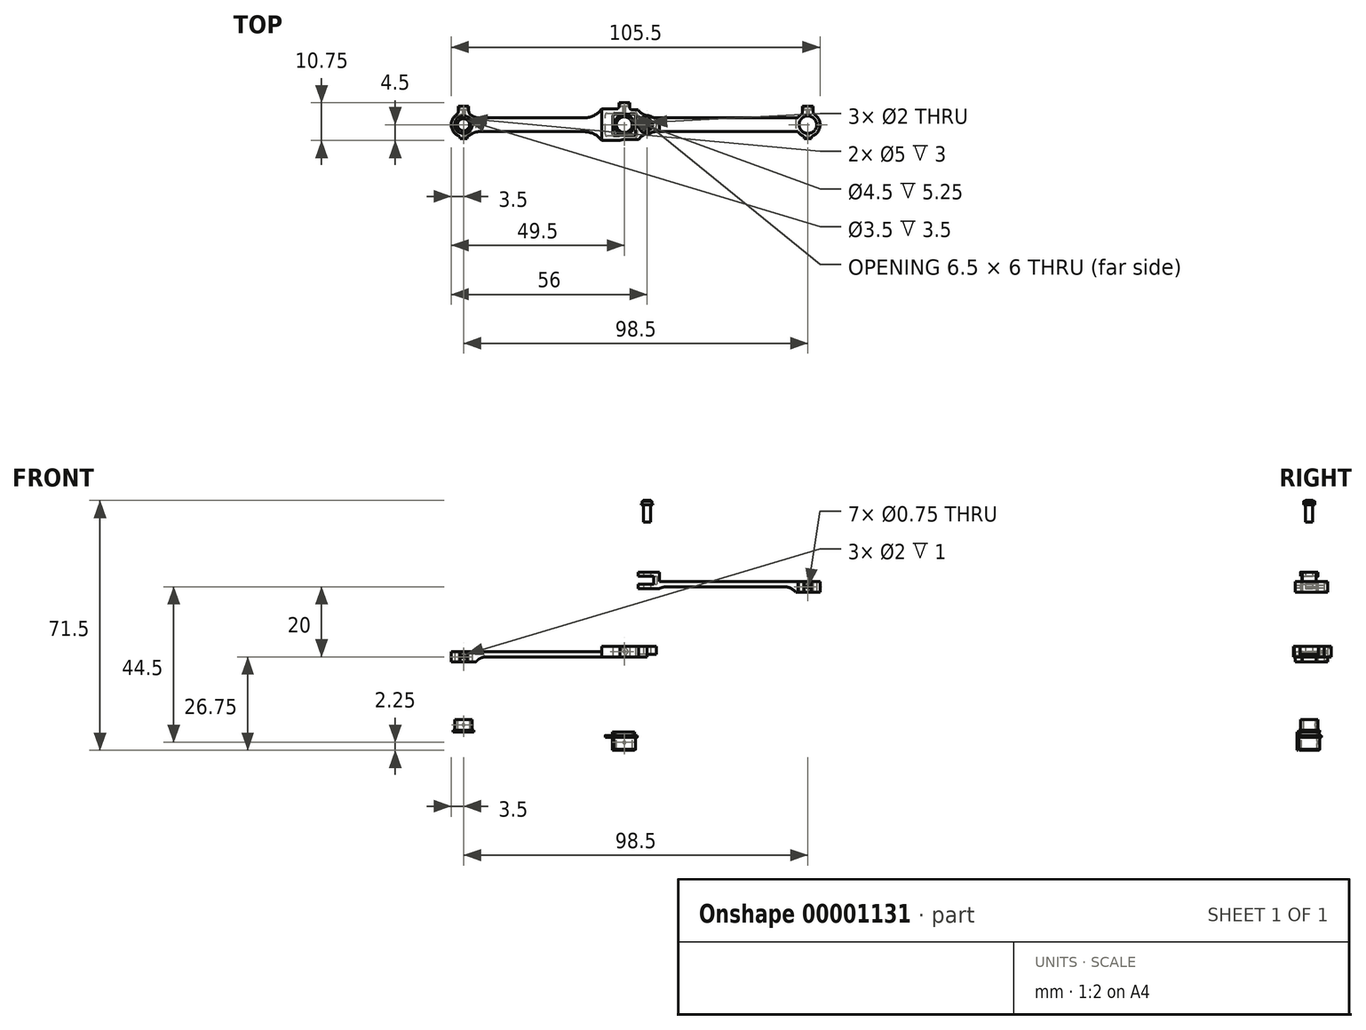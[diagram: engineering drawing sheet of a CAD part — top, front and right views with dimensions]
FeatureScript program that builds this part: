
annotation { "Feature Type Name" : "Feature", "Feature Type Description" : "" }
export const myFeature = defineFeature(function(context is Context, id is Id, definition is map)
    precondition{}
    {
        {
            var Q0;
            Q0=qCreatedBy(makeId("Top.planeOp"),FACE);
            var sketch = newSketch(context, id + "F0", { "sketchPlane" : qUnion([Q0])});
            skCircle(sketch, "E0", {"center": v(0, 0) * mm, "radius": 2.5 * mm});
            skCircle(sketch, "E1", {"center": v(46, 0) * mm, "radius": 2.25 * mm, "construction": true});
            skCircle(sketch, "E2", {"center": v(52.5, 0) * mm, "radius": 1 * mm});
            skArc(sketch, "E3", {"start": v(1, -3.35) * mm, "mid": v(2.05, -2.84) * mm, "end": v(2.87, -2) * mm});
            skCircle(sketch, "E4", {"center": v(52.5, 0) * mm, "radius": 2.62 * mm});
            skLineSegment(sketch, "E5", {"start": v(-1.5, 3.16) * mm, "end": v(-1.5, 5.25) * mm});
            skLineSegment(sketch, "E6", {"start": v(-1.5, 5.25) * mm, "end": v(1.5, 5.25) * mm});
            skLineSegment(sketch, "E7", {"start": v(1.5, 5.25) * mm, "end": v(1.5, 3.16) * mm});
            skLineSegment(sketch, "E8", {"start": v(42.75, 3) * mm, "end": v(49.25, 3) * mm});
            skLineSegment(sketch, "E9", {"start": v(49.25, 3) * mm, "end": v(49.25, -3) * mm});
            skLineSegment(sketch, "E10", {"start": v(49.25, -3) * mm, "end": v(42.75, -3) * mm});
            skLineSegment(sketch, "E11", {"start": v(42.75, -3) * mm, "end": v(42.75, 3) * mm});
            skLineSegment(sketch, "E12", {"start": v(52.5, 2.62) * mm, "end": v(52.5, 4.25) * mm});
            skLineSegment(sketch, "E13", {"start": v(52.5, 4.25) * mm, "end": v(47.5, 4.25) * mm});
            skLineSegment(sketch, "E14", {"start": v(39.5, 4.5) * mm, "end": v(39.5, 2) * mm});
            skLineSegment(sketch, "E15", {"start": v(39.5, -4.5) * mm, "end": v(44.75, -4.5) * mm});
            skLineSegment(sketch, "E16", {"start": v(52.5, -4.5) * mm, "end": v(52.5, -2.62) * mm});
            skLineSegment(sketch, "E17", {"start": v(2.87, 2) * mm, "end": v(39.5, 2) * mm});
            skLineSegment(sketch, "E18", {"start": v(2.87, -2) * mm, "end": v(39.5, -2) * mm});
            skLineSegment(sketch, "E19", {"start": v(44.5, 4.5) * mm, "end": v(44.5, 6.25) * mm});
            skLineSegment(sketch, "E20", {"start": v(44.5, 6.25) * mm, "end": v(47.5, 6.25) * mm});
            skLineSegment(sketch, "E21", {"start": v(47.5, 6.25) * mm, "end": v(47.5, 4.25) * mm});
            skLineSegment(sketch, "E22.trimOffspring", {"start": v(39.5, -2) * mm, "end": v(39.5, -4.5) * mm});
            skLineSegment(sketch, "E23", {"start": v(-1, -3.35) * mm, "end": v(-1, -4) * mm});
            skLineSegment(sketch, "E24", {"start": v(-1, -4) * mm, "end": v(1, -4) * mm});
            skLineSegment(sketch, "E25", {"start": v(1, -4) * mm, "end": v(1, -3.35) * mm});
            skArc(sketch, "E26.trimOffspring", {"start": v(2.87, 2) * mm, "mid": v(2.26, 2.67) * mm, "end": v(1.5, 3.16) * mm});
            skArc(sketch, "E27.trimOffspring", {"start": v(-1.5, 3.16) * mm, "mid": v(-3.49, -0.27) * mm, "end": v(-1, -3.35) * mm});
            skPoint(sketch, "E28", {"position": v(46, 6.25) * mm});
            skArc(sketch, "E29", {"start": v(50, 4.25) * mm, "mid": v(51.07, 3.16) * mm, "end": v(52.5, 2.63) * mm});
            skArc(sketch, "E30", {"start": v(52.5, -2.62) * mm, "mid": v(51.03, -3.27) * mm, "end": v(50, -4.5) * mm});
            skLineSegment(sketch, "E31", {"start": v(39.5, 4.5) * mm, "end": v(44.5, 4.5) * mm});
            skCircle(sketch, "E32", {"center": v(46, 0) * mm, "radius": 3 * mm, "construction": true});
            skLineSegment(sketch, "E33", {"start": v(50.14, -4.25) * mm, "end": v(46, -4.25) * mm});
            skArc(sketch, "E34", {"start": v(46, -4.25) * mm, "mid": v(45.36, -4.31) * mm, "end": v(44.75, -4.5) * mm});
            skLineSegment(sketch, "E35.trimOffspring", {"start": v(50, -4.5) * mm, "end": v(52.5, -4.5) * mm});
            skSolve(sketch);
        }
        {
            var Q0;
            Q0=makeQuery(id+"F0.imprint","IMPRINT",FACE,{"disambiguationData":[TD([[makeQuery(id+"F0.imprint","IMPRINT",EDGE,{"derivedFrom":sQuery(id+"F0.wireOp",EDGE,"E0")}),-1.0]])]});
            extrude(context, id + "F1", {"entities" : qUnion([Q0]), "depth" : 3 * mm});
        }
        {
            var Q0;
            Q0=makeQuery(id+"F1.opExtrude","SWEPT_EDGE",EDGE,{"disambiguationData":[OSD([sQuery(id+"F0.wireOp",EDGE,"E14"),sQuery(id+"F0.wireOp",EDGE,"E17")])]});
            var Q1;
            Q1=makeQuery(id+"F1.opExtrude","SWEPT_EDGE",EDGE,{"disambiguationData":[OSD([sQuery(id+"F0.wireOp",EDGE,"E18"),sQuery(id+"F0.wireOp",EDGE,"E22.trimOffspring")])]});
            fillet(context, id + "F2", {"entities" : qUnion([Q0, Q1]), "radius" : 6 * mm, "tangentPropagation" : true, "allowEdgeOverflow" : false});
        }
        {
            var Q0;
            Q0=makeQuery(id+"F0.imprint","IMPRINT",FACE,{"disambiguationData":[TD([[makeQuery(id+"F0.imprint","IMPRINT",EDGE,{"derivedFrom":sQuery(id+"F0.wireOp",EDGE,"E2")}),-1.0]])]});
            extrude(context, id + "F3", {"entities" : qUnion([Q0]), "operationType" : NewBodyOperationType.ADD, "depth" : 3 * mm});
        }
        {
            var Q0;
            Q0=makeQuery(id+"F1.opExtrude","SWEPT_EDGE",EDGE,{"disambiguationData":[OSD([sQuery(id+"F0.wireOp",EDGE,"E13"),sQuery(id+"F0.wireOp",EDGE,"E21")])]});
            var Q1;
            Q1=makeQuery(id+"F1.opExtrude","SWEPT_EDGE",EDGE,{"disambiguationData":[OSD([sQuery(id+"F0.wireOp",EDGE,"E19"),sQuery(id+"F0.wireOp",EDGE,"E31")])]});
            fillet(context, id + "F4", {"entities" : qUnion([Q0, Q1]), "radius" : 0.75 * mm, "tangentPropagation" : true, "allowEdgeOverflow" : false});
        }
        {
            var Q0;
            Q0=makeQuery(id+"F1.opExtrude","SWEPT_EDGE",EDGE,{"disambiguationData":[OSD([sQuery(id+"F0.wireOp",EDGE,"E3"),sQuery(id+"F0.wireOp",EDGE,"E25")])]});
            var Q1;
            Q1=makeQuery(id+"F1.opExtrude","SWEPT_EDGE",EDGE,{"disambiguationData":[OSD([sQuery(id+"F0.wireOp",EDGE,"E23"),sQuery(id+"F0.wireOp",EDGE,"E27.trimOffspring")])]});
            fillet(context, id + "F5", {"entities" : qUnion([Q0, Q1]), "radius" : 0.75 * mm, "tangentPropagation" : true, "allowEdgeOverflow" : false});
        }
        {
            var Q0;
            Q0=makeQuery(id+"F1.opExtrude","SWEPT_EDGE",EDGE,{"disambiguationData":[OSD([sQuery(id+"F0.wireOp",EDGE,"E7"),sQuery(id+"F0.wireOp",EDGE,"E26.trimOffspring")])]});
            var Q1;
            Q1=makeQuery(id+"F1.opExtrude","SWEPT_EDGE",EDGE,{"disambiguationData":[OSD([sQuery(id+"F0.wireOp",EDGE,"E5"),sQuery(id+"F0.wireOp",EDGE,"E27.trimOffspring")])]});
            fillet(context, id + "F6", {"entities" : qUnion([Q0, Q1]), "radius" : 1.25 * mm, "tangentPropagation" : true, "allowEdgeOverflow" : false});
        }
        {
            var Q0;
            Q0=makeQuery(id+"F1.opExtrude","SWEPT_EDGE",EDGE,{"disambiguationData":[OSD([sQuery(id+"F0.wireOp",EDGE,"E17"),sQuery(id+"F0.wireOp",EDGE,"E26.trimOffspring")])]});
            var Q1;
            Q1=makeQuery(id+"F1.opExtrude","SWEPT_EDGE",EDGE,{"disambiguationData":[OSD([sQuery(id+"F0.wireOp",EDGE,"E3"),sQuery(id+"F0.wireOp",EDGE,"E18")])]});
            fillet(context, id + "F7", {"entities" : qUnion([Q0, Q1]), "radius" : 3.5 * mm, "tangentPropagation" : true, "allowEdgeOverflow" : false});
        }
        {
            var Q0;
            Q0=makeQuery(id+"F1.opExtrude","SWEPT_EDGE",EDGE,{"disambiguationData":[OSD([sQuery(id+"F0.wireOp",EDGE,"E8"),sQuery(id+"F0.wireOp",EDGE,"E11")])]});
            var Q1;
            Q1=makeQuery(id+"F1.opExtrude","SWEPT_EDGE",EDGE,{"disambiguationData":[OSD([sQuery(id+"F0.wireOp",EDGE,"E8"),sQuery(id+"F0.wireOp",EDGE,"E9")])]});
            var Q2;
            Q2=makeQuery(id+"F1.opExtrude","SWEPT_EDGE",EDGE,{"disambiguationData":[OSD([sQuery(id+"F0.wireOp",EDGE,"E10"),sQuery(id+"F0.wireOp",EDGE,"E11")])]});
            var Q3;
            Q3=makeQuery(id+"F1.opExtrude","SWEPT_EDGE",EDGE,{"disambiguationData":[OSD([sQuery(id+"F0.wireOp",EDGE,"E9"),sQuery(id+"F0.wireOp",EDGE,"E10")])]});
            fillet(context, id + "F8", {"entities" : qUnion([Q0, Q1, Q2, Q3]), "radius" : 0.5 * mm, "tangentPropagation" : true, "allowEdgeOverflow" : false});
        }
        {
            var Q0;
            {var subQ0=sQuery(id+"F0.wireOp",EDGE,"E4");Q0=makeQuery(id+"F3.boolean.opBoolean","MERGE",FACE,{"derivedFrom":[makeQuery(id+"F1.opExtrude","CAP_FACE",FACE,{"disambiguationData":[OSD([sQuery(id+"F0.wireOp",EDGE,"E0"),sQuery(id+"F0.wireOp",EDGE,"E3"),subQ0,sQuery(id+"F0.wireOp",EDGE,"E5"),sQuery(id+"F0.wireOp",EDGE,"E6"),sQuery(id+"F0.wireOp",EDGE,"E7"),sQuery(id+"F0.wireOp",EDGE,"E8"),sQuery(id+"F0.wireOp",EDGE,"E9"),sQuery(id+"F0.wireOp",EDGE,"E10"),sQuery(id+"F0.wireOp",EDGE,"E11"),sQuery(id+"F0.wireOp",EDGE,"E13"),sQuery(id+"F0.wireOp",EDGE,"E14"),sQuery(id+"F0.wireOp",EDGE,"E15"),sQuery(id+"F0.wireOp",EDGE,"E17"),sQuery(id+"F0.wireOp",EDGE,"E18"),sQuery(id+"F0.wireOp",EDGE,"E19"),sQuery(id+"F0.wireOp",EDGE,"E20"),sQuery(id+"F0.wireOp",EDGE,"E21"),sQuery(id+"F0.wireOp",EDGE,"E22.trimOffspring"),sQuery(id+"F0.wireOp",EDGE,"E23"),sQuery(id+"F0.wireOp",EDGE,"E24"),sQuery(id+"F0.wireOp",EDGE,"E25"),sQuery(id+"F0.wireOp",EDGE,"E26.trimOffspring"),sQuery(id+"F0.wireOp",EDGE,"E27.trimOffspring"),sQuery(id+"F0.wireOp",EDGE,"E29"),sQuery(id+"F0.wireOp",EDGE,"E30"),sQuery(id+"F0.wireOp",EDGE,"E31"),sQuery(id+"F0.wireOp",EDGE,"E33"),sQuery(id+"F0.wireOp",EDGE,"E34")])],"isStart":true}),makeQuery(id+"F3.opExtrude","CAP_FACE",FACE,{"disambiguationData":[OSD([sQuery(id+"F0.wireOp",EDGE,"E2"),subQ0])],"isStart":true})]});}
            var sketch = newSketch(context, id + "F9", { "sketchPlane" : qUnion([Q0])});
            skLineSegment(sketch, "E36", {"start": v(3.5, -2.1) * mm, "end": v(3.5, 2.1) * mm});
            skSolve(sketch);
        }
        {
            var Q0;
            {var subQ26=sQuery(id+"F9.wireOp",EDGE,"E36");Q0=makeQuery(id+"F9.imprint","IMPRINT",FACE,{"disambiguationData":[TD([[makeQuery(id+"F9.imprint","IMPRINT",EDGE,{"derivedFrom":subQ26}),-1.0]])]});}
            extrude(context, id + "F10", {"entities" : qUnion([Q0]), "operationType" : NewBodyOperationType.REMOVE, "oppositeDirection" : true, "depth" : 1.5 * mm});
        }
        {
            var Q0;
            {var subQ0=sQuery(id+"F0.wireOp",EDGE,"E4");Q0=makeQuery(id+"F3.boolean.opBoolean","MERGE",FACE,{"derivedFrom":[makeQuery(id+"F1.opExtrude","CAP_FACE",FACE,{"disambiguationData":[OSD([sQuery(id+"F0.wireOp",EDGE,"E0"),sQuery(id+"F0.wireOp",EDGE,"E3"),subQ0,sQuery(id+"F0.wireOp",EDGE,"E5"),sQuery(id+"F0.wireOp",EDGE,"E6"),sQuery(id+"F0.wireOp",EDGE,"E7"),sQuery(id+"F0.wireOp",EDGE,"E8"),sQuery(id+"F0.wireOp",EDGE,"E9"),sQuery(id+"F0.wireOp",EDGE,"E10"),sQuery(id+"F0.wireOp",EDGE,"E11"),sQuery(id+"F0.wireOp",EDGE,"E13"),sQuery(id+"F0.wireOp",EDGE,"E14"),sQuery(id+"F0.wireOp",EDGE,"E15"),sQuery(id+"F0.wireOp",EDGE,"E17"),sQuery(id+"F0.wireOp",EDGE,"E18"),sQuery(id+"F0.wireOp",EDGE,"E19"),sQuery(id+"F0.wireOp",EDGE,"E20"),sQuery(id+"F0.wireOp",EDGE,"E21"),sQuery(id+"F0.wireOp",EDGE,"E22.trimOffspring"),sQuery(id+"F0.wireOp",EDGE,"E23"),sQuery(id+"F0.wireOp",EDGE,"E24"),sQuery(id+"F0.wireOp",EDGE,"E25"),sQuery(id+"F0.wireOp",EDGE,"E26.trimOffspring"),sQuery(id+"F0.wireOp",EDGE,"E27.trimOffspring"),sQuery(id+"F0.wireOp",EDGE,"E29"),sQuery(id+"F0.wireOp",EDGE,"E30"),sQuery(id+"F0.wireOp",EDGE,"E31"),sQuery(id+"F0.wireOp",EDGE,"E33"),sQuery(id+"F0.wireOp",EDGE,"E34")])],"isStart":false}),makeQuery(id+"F3.opExtrude","CAP_FACE",FACE,{"disambiguationData":[OSD([sQuery(id+"F0.wireOp",EDGE,"E2"),subQ0])],"isStart":false})]});}
            var sketch = newSketch(context, id + "F11", { "sketchPlane" : qUnion([Q0])});
            skLineSegment(sketch, "E37", {"start": v(39.5, -4.5) * mm, "end": v(39.5, 4.5) * mm});
            skSolve(sketch);
        }
        {
            var Q0;
            Q0=makeQuery(id+"F11.imprint","IMPRINT",FACE,{"disambiguationData":[TD([[makeQuery(id+"F11.imprint","IMPRINT",EDGE,{"derivedFrom":sQuery(id+"F11.wireOp",EDGE,"E37")}),-1.0]])]});
            extrude(context, id + "F12", {"entities" : qUnion([Q0]), "operationType" : NewBodyOperationType.ADD, "depth" : 1.5 * mm});
        }
        {
            var Q0;
            Q0=makeQuery(id+"F10.boolean.opBoolean","COPY",EDGE,{"derivedFrom":makeQuery(id+"F10.opExtrude","CAP_EDGE",EDGE,{"disambiguationData":[OSD([sQuery(id+"F9.wireOp",EDGE,"E36")])],"isStart":false})});
            var Q1;
            Q1=makeQuery(id+"F12.opExtrude","CAP_EDGE",EDGE,{"disambiguationData":[OSD([sQuery(id+"F11.wireOp",EDGE,"E37")])],"isStart":true});
            fillet(context, id + "F13", {"entities" : qUnion([Q0, Q1]), "radius" : 4 * mm, "tangentPropagation" : true, "allowEdgeOverflow" : false});
        }
        {
            var Q0;
            Q0=makeQuery(id+"F0.imprint","IMPRINT",FACE,{"disambiguationData":[TD([[makeQuery(id+"F0.imprint","IMPRINT",EDGE,{"derivedFrom":sQuery(id+"F0.wireOp",EDGE,"E2")}),-1.0]])]});
            extrude(context, id + "F14", {"entities" : qUnion([Q0]), "operationType" : NewBodyOperationType.REMOVE, "depth" : 2.25 * mm});
        }
        {
            var Q0;
            Q0=makeQuery(id+"F1.opExtrude","SWEPT_FACE",FACE,{"disambiguationData":[OSD([sQuery(id+"F0.wireOp",EDGE,"E6")])]});
            var sketch = newSketch(context, id + "F15", { "sketchPlane" : qUnion([Q0])});
            skPoint(sketch, "E38", {"position": v(1.5, 1.5) * mm});
            skPoint(sketch, "E39", {"position": v(0, 0) * mm});
            skCircle(sketch, "E40", {"center": v(0, 1.5) * mm, "radius": 1 * mm});
            skSolve(sketch);
        }
        {
            var Q0;
            Q0=makeQuery(id+"F15.imprint","IMPRINT",FACE,{"disambiguationData":[TD([[makeQuery(id+"F15.imprint","IMPRINT",EDGE,{"derivedFrom":sQuery(id+"F15.wireOp",EDGE,"E40")}),1.0]])]});
            extrude(context, id + "F16", {"entities" : qUnion([Q0]), "operationType" : NewBodyOperationType.REMOVE, "oppositeDirection" : true, "depth" : 1 * mm});
        }
        {
            var Q0;
            {var subQ0=sQuery(id+"F0.wireOp",EDGE,"E20");Q0=makeQuery(id+"F12.boolean.opBoolean","MERGE",FACE,{"derivedFrom":[makeQuery(id+"F1.opExtrude","SWEPT_FACE",FACE,{"disambiguationData":[OSD([subQ0])]}),makeQuery(id+"F12.opExtrude","SWEPT_FACE",FACE,{"disambiguationData":[OSD([subQ0])]})]});}
            var sketch = newSketch(context, id + "F17", { "sketchPlane" : qUnion([Q0])});
            skPoint(sketch, "E41", {"position": v(-46, 1.5) * mm});
            skPoint(sketch, "E42", {"position": v(-44.5, 3) * mm});
            skCircle(sketch, "E43", {"center": v(-46, 3) * mm, "radius": 1 * mm});
            skCircle(sketch, "E44", {"center": v(-46, 3) * mm, "radius": 0.38 * mm});
            skSolve(sketch);
        }
        {
            var Q0;
            Q0=makeQuery(id+"F17.imprint","IMPRINT",FACE,{"disambiguationData":[TD([[makeQuery(id+"F17.imprint","IMPRINT",EDGE,{"derivedFrom":sQuery(id+"F17.wireOp",EDGE,"E43")}),1.0]])]});
            extrude(context, id + "F18", {"entities" : qUnion([Q0]), "operationType" : NewBodyOperationType.REMOVE, "oppositeDirection" : true, "depth" : 1 * mm});
        }
        {
            var Q0;
            Q0=makeQuery(id+"F1.opExtrude","SWEPT_FACE",FACE,{"disambiguationData":[OSD([sQuery(id+"F0.wireOp",EDGE,"E24")])]});
            var sketch = newSketch(context, id + "F19", { "sketchPlane" : qUnion([Q0])});
            skPoint(sketch, "E45", {"position": v(-1, 1.5) * mm});
            skPoint(sketch, "E46", {"position": v(0, 3) * mm});
            skCircle(sketch, "E47", {"center": v(0, 1.5) * mm, "radius": 0.38 * mm});
            skSolve(sketch);
        }
        {
            var Q0;
            Q0=makeQuery(id+"F19.imprint","IMPRINT",FACE,{"disambiguationData":[TD([[makeQuery(id+"F19.imprint","IMPRINT",EDGE,{"derivedFrom":sQuery(id+"F19.wireOp",EDGE,"E47")}),1.0]])]});
            extrude(context, id + "F20", {"entities" : qUnion([Q0]), "operationType" : NewBodyOperationType.REMOVE, "oppositeDirection" : true, "depth" : 25 * mm});
        }
        {
            var Q0;
            {var subQ0=sQuery(id+"F0.wireOp",EDGE,"E20");Q0=makeQuery(id+"F18.boolean.opBoolean","SPLIT",FACE,{"disambiguationData":[TD([makeQuery(id+"F18.opExtrude","SWEPT_FACE",FACE,{"disambiguationData":[OSD([sQuery(id+"F17.wireOp",EDGE,"E44")])]})])],"derivedFrom":makeQuery(id+"F12.boolean.opBoolean","MERGE",FACE,{"derivedFrom":[makeQuery(id+"F1.opExtrude","SWEPT_FACE",FACE,{"disambiguationData":[OSD([subQ0])]}),makeQuery(id+"F12.opExtrude","SWEPT_FACE",FACE,{"disambiguationData":[OSD([subQ0])]})]})});}
            extrude(context, id + "F21", {"entities" : qUnion([Q0]), "operationType" : NewBodyOperationType.REMOVE, "endBound" : BoundingType.UP_TO_NEXT, "oppositeDirection" : true, "depth" : 25 * mm});
        }
        {
            var Q0;
            Q0=qCreatedBy(makeId("Top.planeOp"),FACE);
            cPlane(context, id + "F22", {"entities" : qUnion([Q0]), "cplaneType" : CPlaneType.OFFSET, "offset" : 20 * mm, "width" : 150 * mm, "height" : 150 * mm});
        }
        {
            var Q0;
            Q0=qCreatedBy(makeId("Top.planeOp"),FACE);
            cPlane(context, id + "F23", {"entities" : qUnion([Q0]), "cplaneType" : CPlaneType.OFFSET, "offset" : 20 * mm, "oppositeDirection" : true, "width" : 150 * mm, "height" : 150 * mm});
        }
        {
            var Q0;
            Q0=qCreatedBy(id+"F23.planeOp",FACE);
            var sketch = newSketch(context, id + "F24", { "sketchPlane" : qUnion([Q0])});
            skCircle(sketch, "E48", {"center": v(0, 0) * mm, "radius": 3 * mm});
            skCircle(sketch, "E49", {"center": v(0, 0) * mm, "radius": 2.5 * mm});
            skCircle(sketch, "E50", {"center": v(0, 0) * mm, "radius": 1.75 * mm});
            skSolve(sketch);
        }
        {
            var Q0;
            Q0=makeQuery(id+"F24.imprint","IMPRINT",FACE,{"disambiguationData":[TD([[makeQuery(id+"F24.imprint","IMPRINT",EDGE,{"derivedFrom":sQuery(id+"F24.wireOp",EDGE,"E49")}),1.0]])]});
            extrude(context, id + "F25", {"entities" : qUnion([Q0]), "depth" : 3.5 * mm});
        }
        {
            var Q0;
            Q0=makeQuery(id+"F24.imprint","IMPRINT",FACE,{"disambiguationData":[TD([[makeQuery(id+"F24.imprint","IMPRINT",EDGE,{"derivedFrom":sQuery(id+"F24.wireOp",EDGE,"E48")}),1.0]])]});
            extrude(context, id + "F26", {"entities" : qUnion([Q0]), "operationType" : NewBodyOperationType.ADD, "depth" : 0.5 * mm});
        }
        {
            var Q0;
            Q0=qCreatedBy(makeId("Front.planeOp"),FACE);
            var sketch = newSketch(context, id + "F27", { "sketchPlane" : qUnion([Q0])});
            skLineSegment(sketch, "E51", {"start": v(0, 0) * mm, "end": v(0, -18) * mm, "construction": true});
            skCircle(sketch, "E52", {"center": v(0, -18) * mm, "radius": 0.38 * mm});
            skSolve(sketch);
        }
        {
            var Q0;
            Q0=makeQuery(id+"F27.imprint","IMPRINT",FACE,{"disambiguationData":[TD([[makeQuery(id+"F27.imprint","IMPRINT",EDGE,{"derivedFrom":sQuery(id+"F27.wireOp",EDGE,"E52")}),1.0]])]});
            extrude(context, id + "F28", {"entities" : qUnion([Q0]), "operationType" : NewBodyOperationType.REMOVE, "oppositeDirection" : true, "depth" : 25 * mm});
        }
        {
            var Q0;
            Q0=qCreatedBy(id+"F22.planeOp",FACE);
            var sketch = newSketch(context, id + "F29", { "sketchPlane" : qUnion([Q0])});
            skLineSegment(sketch, "E53", {"start": v(0, 0) * mm, "end": v(52.5, 0) * mm, "construction": true});
            skLineSegment(sketch, "E54", {"start": v(52.5, 0) * mm, "end": v(98.5, 0) * mm, "construction": true});
            skCircle(sketch, "E55", {"center": v(52.5, 0) * mm, "radius": 1 * mm});
            skCircle(sketch, "E56", {"center": v(98.5, 0) * mm, "radius": 2.5 * mm});
            skArc(sketch, "E57", {"start": v(54, 2) * mm, "mid": v(50, 0) * mm, "end": v(54, -2) * mm});
            skArc(sketch, "E58", {"start": v(95.63, -2) * mm, "mid": v(96.45, -2.84) * mm, "end": v(97.5, -3.35) * mm});
            skLineSegment(sketch, "E59", {"start": v(54, 2) * mm, "end": v(95.63, 2) * mm});
            skLineSegment(sketch, "E60", {"start": v(54, -2) * mm, "end": v(95.63, -2) * mm});
            skLineSegment(sketch, "E61", {"start": v(97.5, -3.35) * mm, "end": v(97.5, -4) * mm});
            skLineSegment(sketch, "E62", {"start": v(97.5, -4) * mm, "end": v(99.5, -4) * mm});
            skLineSegment(sketch, "E63", {"start": v(99.5, -4) * mm, "end": v(99.5, -3.35) * mm});
            skLineSegment(sketch, "E64", {"start": v(97, 3.16) * mm, "end": v(97, 5.25) * mm});
            skLineSegment(sketch, "E65", {"start": v(97, 5.25) * mm, "end": v(100, 5.25) * mm});
            skLineSegment(sketch, "E66", {"start": v(100, 5.25) * mm, "end": v(100, 3.16) * mm});
            skPoint(sketch, "E67", {"position": v(98.5, -4) * mm});
            skPoint(sketch, "E68", {"position": v(98.5, 5.25) * mm});
            skArc(sketch, "E69.trimOffspring", {"start": v(99.5, -3.35) * mm, "mid": v(101.99, -0.27) * mm, "end": v(100, 3.16) * mm});
            skArc(sketch, "E70.trimOffspring", {"start": v(97, 3.16) * mm, "mid": v(96.24, 2.67) * mm, "end": v(95.63, 2) * mm});
            skSolve(sketch);
        }
        {
            var Q0;
            Q0=makeQuery(id+"F29.imprint","IMPRINT",FACE,{"disambiguationData":[TD([[makeQuery(id+"F29.imprint","IMPRINT",EDGE,{"derivedFrom":sQuery(id+"F29.wireOp",EDGE,"E55")}),-1.0]])]});
            extrude(context, id + "F30", {"entities" : qUnion([Q0]), "depth" : 3 * mm});
        }
        {
            var Q0;
            Q0=makeQuery(id+"F29.imprint","IMPRINT",FACE,{"disambiguationData":[TD([[makeQuery(id+"F29.imprint","IMPRINT",EDGE,{"derivedFrom":sQuery(id+"F29.wireOp",EDGE,"E55")}),-1.0]])]});
            var sketch = newSketch(context, id + "F31", { "sketchPlane" : qUnion([Q0])});
            skLineSegment(sketch, "E71", {"start": v(95, 2) * mm, "end": v(95, -2) * mm});
            skLineSegment(sketch, "E72", {"start": v(56, 2) * mm, "end": v(56, -2) * mm});
            skSolve(sketch);
        }
        {
            var Q0;
            {var subQ2=sQuery(id+"F31.wireOp",EDGE,"E71");Q0=makeQuery(id+"F31.imprint","IMPRINT",FACE,{"disambiguationData":[TD([[makeQuery(id+"F31.imprint","IMPRINT",EDGE,{"derivedFrom":subQ2}),-1.0]])]});}
            extrude(context, id + "F32", {"entities" : qUnion([Q0]), "operationType" : NewBodyOperationType.REMOVE, "depth" : 1.5 * mm});
        }
        {
            var Q0;
            Q0=makeQuery(id+"F30.opExtrude","CAP_FACE",FACE,{"disambiguationData":[OSD([sQuery(id+"F29.wireOp",EDGE,"E55"),sQuery(id+"F29.wireOp",EDGE,"E56"),sQuery(id+"F29.wireOp",EDGE,"E57"),sQuery(id+"F29.wireOp",EDGE,"E58"),sQuery(id+"F29.wireOp",EDGE,"E59"),sQuery(id+"F29.wireOp",EDGE,"E60"),sQuery(id+"F29.wireOp",EDGE,"E61"),sQuery(id+"F29.wireOp",EDGE,"E62"),sQuery(id+"F29.wireOp",EDGE,"E63"),sQuery(id+"F29.wireOp",EDGE,"E64"),sQuery(id+"F29.wireOp",EDGE,"E65"),sQuery(id+"F29.wireOp",EDGE,"E66"),sQuery(id+"F29.wireOp",EDGE,"E69.trimOffspring"),sQuery(id+"F29.wireOp",EDGE,"E70.trimOffspring")])],"isStart":false});
            var sketch = newSketch(context, id + "F33", { "sketchPlane" : qUnion([Q0])});
            skLineSegment(sketch, "E73", {"start": v(56, -2) * mm, "end": v(56, 2) * mm});
            skSolve(sketch);
        }
        {
            var Q0;
            {var subQ0=sQuery(id+"F29.wireOp",EDGE,"E55");var subQ1=sQuery(id+"F29.wireOp",EDGE,"E57");var subQ2=sQuery(id+"F29.wireOp",EDGE,"E59");var subQ3=sQuery(id+"F29.wireOp",EDGE,"E60");Q0=makeQuery(id+"F32.boolean.opBoolean","SPLIT",FACE,{"disambiguationData":[TD([makeQuery(id+"F30.opExtrude","SWEPT_FACE",FACE,{"disambiguationData":[OSD([subQ0])]})])],"derivedFrom":makeQuery(id+"F30.opExtrude","CAP_FACE",FACE,{"disambiguationData":[OSD([subQ0,sQuery(id+"F29.wireOp",EDGE,"E56"),subQ1,sQuery(id+"F29.wireOp",EDGE,"E58"),subQ2,subQ3,sQuery(id+"F29.wireOp",EDGE,"E61"),sQuery(id+"F29.wireOp",EDGE,"E62"),sQuery(id+"F29.wireOp",EDGE,"E63"),sQuery(id+"F29.wireOp",EDGE,"E64"),sQuery(id+"F29.wireOp",EDGE,"E65"),sQuery(id+"F29.wireOp",EDGE,"E66"),sQuery(id+"F29.wireOp",EDGE,"E69.trimOffspring"),sQuery(id+"F29.wireOp",EDGE,"E70.trimOffspring")])],"isStart":true})});}
            extrude(context, id + "F34", {"entities" : qUnion([Q0]), "operationType" : NewBodyOperationType.REMOVE, "oppositeDirection" : true, "depth" : 1 * mm});
        }
        {
            var Q0;
            {var subQ1=sQuery(id+"F33.wireOp",EDGE,"E73");Q0=makeQuery(id+"F33.imprint","IMPRINT",FACE,{"disambiguationData":[TD([[makeQuery(id+"F33.imprint","IMPRINT",EDGE,{"derivedFrom":subQ1}),1.0]])]});}
            extrude(context, id + "F35", {"entities" : qUnion([Q0]), "operationType" : NewBodyOperationType.ADD, "depth" : 2.75 * mm});
        }
        {
            var Q0;
            Q0=makeQuery(id+"F32.boolean.opBoolean","COPY",EDGE,{"derivedFrom":makeQuery(id+"F32.opExtrude","CAP_EDGE",EDGE,{"disambiguationData":[OSD([sQuery(id+"F31.wireOp",EDGE,"E72")])],"isStart":false})});
            var Q1;
            Q1=makeQuery(id+"F32.boolean.opBoolean","COPY",EDGE,{"derivedFrom":makeQuery(id+"F32.opExtrude","CAP_EDGE",EDGE,{"disambiguationData":[OSD([sQuery(id+"F31.wireOp",EDGE,"E71")])],"isStart":false})});
            var Q2;
            Q2=makeQuery(id+"F35.opExtrude","CAP_EDGE",EDGE,{"disambiguationData":[OSD([sQuery(id+"F33.wireOp",EDGE,"E73")])],"isStart":true});
            fillet(context, id + "F36", {"entities" : qUnion([Q0, Q1, Q2]), "radius" : 4 * mm, "tangentPropagation" : true, "allowEdgeOverflow" : false});
        }
        {
            var Q0;
            Q0=makeQuery(id+"F30.opExtrude","CAP_FACE",FACE,{"disambiguationData":[OSD([sQuery(id+"F29.wireOp",EDGE,"E55"),sQuery(id+"F29.wireOp",EDGE,"E56"),sQuery(id+"F29.wireOp",EDGE,"E57"),sQuery(id+"F29.wireOp",EDGE,"E58"),sQuery(id+"F29.wireOp",EDGE,"E59"),sQuery(id+"F29.wireOp",EDGE,"E60"),sQuery(id+"F29.wireOp",EDGE,"E61"),sQuery(id+"F29.wireOp",EDGE,"E62"),sQuery(id+"F29.wireOp",EDGE,"E63"),sQuery(id+"F29.wireOp",EDGE,"E64"),sQuery(id+"F29.wireOp",EDGE,"E65"),sQuery(id+"F29.wireOp",EDGE,"E66"),sQuery(id+"F29.wireOp",EDGE,"E69.trimOffspring"),sQuery(id+"F29.wireOp",EDGE,"E70.trimOffspring")])],"isStart":false});
            var sketch = newSketch(context, id + "F37", { "sketchPlane" : qUnion([Q0])});
            skCircle(sketch, "E74", {"center": v(52.5, 0) * mm, "radius": 2.75 * mm});
            skSolve(sketch);
        }
        {
            var Q0;
            Q0=makeQuery(id+"F37.imprint","IMPRINT",FACE,{"disambiguationData":[TD([[makeQuery(id+"F37.imprint","IMPRINT",EDGE,{"derivedFrom":sQuery(id+"F37.wireOp",EDGE,"E74")}),1.0]])]});
            extrude(context, id + "F38", {"entities" : qUnion([Q0]), "operationType" : NewBodyOperationType.REMOVE, "depth" : 1.5 * mm});
        }
        {
            var Q0;
            Q0=makeQuery(id+"F37.imprint","IMPRINT",FACE,{"disambiguationData":[TD([[makeQuery(id+"F37.imprint","IMPRINT",EDGE,{"derivedFrom":sQuery(id+"F37.wireOp",EDGE,"E74")}),1.0]])]});
            extrude(context, id + "F39", {"entities" : qUnion([Q0]), "operationType" : NewBodyOperationType.REMOVE, "oppositeDirection" : true, "depth" : 0.75 * mm});
        }
        {
            var Q0;
            Q0=makeQuery(id+"F30.opExtrude","SWEPT_EDGE",EDGE,{"disambiguationData":[OSD([sQuery(id+"F29.wireOp",EDGE,"E58"),sQuery(id+"F29.wireOp",EDGE,"E61")])]});
            var Q1;
            Q1=makeQuery(id+"F30.opExtrude","SWEPT_EDGE",EDGE,{"disambiguationData":[OSD([sQuery(id+"F29.wireOp",EDGE,"E63"),sQuery(id+"F29.wireOp",EDGE,"E69.trimOffspring")])]});
            fillet(context, id + "F40", {"entities" : qUnion([Q0, Q1]), "radius" : 0.75 * mm, "tangentPropagation" : true, "allowEdgeOverflow" : false});
        }
        {
            var Q0;
            Q0=makeQuery(id+"F30.opExtrude","SWEPT_EDGE",EDGE,{"disambiguationData":[OSD([sQuery(id+"F29.wireOp",EDGE,"E66"),sQuery(id+"F29.wireOp",EDGE,"E69.trimOffspring")])]});
            var Q1;
            Q1=makeQuery(id+"F30.opExtrude","SWEPT_EDGE",EDGE,{"disambiguationData":[OSD([sQuery(id+"F29.wireOp",EDGE,"E64"),sQuery(id+"F29.wireOp",EDGE,"E70.trimOffspring")])]});
            fillet(context, id + "F41", {"entities" : qUnion([Q0, Q1]), "radius" : 1.25 * mm, "tangentPropagation" : true, "allowEdgeOverflow" : false});
        }
        {
            var Q0;
            {var subQ0=sQuery(id+"F29.wireOp",EDGE,"E57");var subQ1=sQuery(id+"F29.wireOp",EDGE,"E59");Q0=makeQuery(id+"F38.boolean.opBoolean","SPLIT",EDGE,{"disambiguationData":[TD([makeQuery(id+"F38.opExtrude","CAP_FACE",FACE,{"disambiguationData":[OSD([sQuery(id+"F37.wireOp",EDGE,"E74")])],"isStart":false})])],"derivedFrom":makeQuery(id+"F35.boolean.opBoolean","MERGE",EDGE,{"derivedFrom":[makeQuery(id+"F30.opExtrude","SWEPT_EDGE",EDGE,{"disambiguationData":[OSD([subQ0,subQ1])]}),makeQuery(id+"F35.opExtrude","SWEPT_EDGE",EDGE,{"disambiguationData":[OSD([subQ0,subQ1])]})]})});}
            var Q1;
            {var subQ0=sQuery(id+"F29.wireOp",EDGE,"E57");var subQ1=sQuery(id+"F29.wireOp",EDGE,"E60");Q1=makeQuery(id+"F38.boolean.opBoolean","SPLIT",EDGE,{"disambiguationData":[TD([makeQuery(id+"F38.opExtrude","CAP_FACE",FACE,{"disambiguationData":[OSD([sQuery(id+"F37.wireOp",EDGE,"E74")])],"isStart":false})])],"derivedFrom":makeQuery(id+"F35.boolean.opBoolean","MERGE",EDGE,{"derivedFrom":[makeQuery(id+"F30.opExtrude","SWEPT_EDGE",EDGE,{"disambiguationData":[OSD([subQ0,subQ1])]}),makeQuery(id+"F35.opExtrude","SWEPT_EDGE",EDGE,{"disambiguationData":[OSD([subQ0,subQ1])]})]})});}
            fillet(context, id + "F42", {"entities" : qUnion([Q0, Q1]), "radius" : 3.5 * mm, "tangentPropagation" : true, "allowEdgeOverflow" : false});
        }
        {
            var Q0;
            Q0=makeQuery(id+"F30.opExtrude","SWEPT_FACE",FACE,{"disambiguationData":[OSD([sQuery(id+"F29.wireOp",EDGE,"E65")])]});
            var sketch = newSketch(context, id + "F43", { "sketchPlane" : qUnion([Q0])});
            skPoint(sketch, "E75", {"position": v(-98.5, 23) * mm});
            skPoint(sketch, "E76", {"position": v(-100, 21.5) * mm});
            skCircle(sketch, "E77", {"center": v(-98.5, 21.5) * mm, "radius": 1 * mm});
            skSolve(sketch);
        }
        {
            var Q0;
            Q0=makeQuery(id+"F43.imprint","IMPRINT",FACE,{"disambiguationData":[TD([[makeQuery(id+"F43.imprint","IMPRINT",EDGE,{"derivedFrom":sQuery(id+"F43.wireOp",EDGE,"E77")}),1.0]])]});
            extrude(context, id + "F44", {"entities" : qUnion([Q0]), "operationType" : NewBodyOperationType.REMOVE, "oppositeDirection" : true, "depth" : 1 * mm});
        }
        {
            var Q0;
            Q0=makeQuery(id+"F30.opExtrude","SWEPT_FACE",FACE,{"disambiguationData":[OSD([sQuery(id+"F29.wireOp",EDGE,"E62")])]});
            var sketch = newSketch(context, id + "F45", { "sketchPlane" : qUnion([Q0])});
            skPoint(sketch, "E78", {"position": v(99.5, 21.5) * mm});
            skPoint(sketch, "E79", {"position": v(98.5, 20) * mm});
            skCircle(sketch, "E80", {"center": v(98.5, 21.5) * mm, "radius": 0.38 * mm});
            skSolve(sketch);
        }
        {
            var Q0;
            Q0=makeQuery(id+"F45.imprint","IMPRINT",FACE,{"disambiguationData":[TD([[makeQuery(id+"F45.imprint","IMPRINT",EDGE,{"derivedFrom":sQuery(id+"F45.wireOp",EDGE,"E80")}),1.0]])]});
            extrude(context, id + "F46", {"entities" : qUnion([Q0]), "operationType" : NewBodyOperationType.REMOVE, "endBound" : BoundingType.THROUGH_ALL, "oppositeDirection" : true, "depth" : 25 * mm});
        }
        {
            var Q0;
            Q0=qCreatedBy(id+"F23.planeOp",FACE);
            var sketch = newSketch(context, id + "F47", { "sketchPlane" : qUnion([Q0])});
            skLineSegment(sketch, "E81", {"start": v(0, 0) * mm, "end": v(46, 0) * mm, "construction": true});
            skCircle(sketch, "E82", {"center": v(46, 0) * mm, "radius": 2.25 * mm});
            skLineSegment(sketch, "E83", {"start": v(40.5, 0) * mm, "end": v(40.5, 3.25) * mm});
            skLineSegment(sketch, "E84", {"start": v(40.5, 3.25) * mm, "end": v(43, 3.25) * mm});
            skLineSegment(sketch, "E85", {"start": v(43, 3.25) * mm, "end": v(43, 3.5) * mm});
            skLineSegment(sketch, "E86", {"start": v(43, 3.5) * mm, "end": v(49.75, 3.5) * mm});
            skLineSegment(sketch, "E87", {"start": v(49.75, 3.5) * mm, "end": v(49.75, -3.5) * mm});
            skLineSegment(sketch, "E88", {"start": v(49.75, -3.5) * mm, "end": v(43, -3.5) * mm});
            skLineSegment(sketch, "E89", {"start": v(43, -3.5) * mm, "end": v(43, -3.25) * mm});
            skLineSegment(sketch, "E90", {"start": v(43, -3.25) * mm, "end": v(40.5, -3.25) * mm});
            skLineSegment(sketch, "E91", {"start": v(40.5, -3.25) * mm, "end": v(40.5, 0) * mm});
            skLineSegment(sketch, "E92", {"start": v(42.75, 3) * mm, "end": v(49.25, 3) * mm});
            skLineSegment(sketch, "E93", {"start": v(49.25, 3) * mm, "end": v(49.25, -3) * mm});
            skLineSegment(sketch, "E94", {"start": v(49.25, -3) * mm, "end": v(42.75, -3) * mm});
            skLineSegment(sketch, "E95", {"start": v(42.75, -3) * mm, "end": v(42.75, 3) * mm});
            skPoint(sketch, "E96", {"position": v(46, 3) * mm});
            skPoint(sketch, "E97", {"position": v(42.75, 0) * mm});
            skCircle(sketch, "E98", {"center": v(46, 0) * mm, "radius": 2.88 * mm});
            skSolve(sketch);
        }
        {
            var Q0;
            Q0=makeQuery(id+"F47.imprint","IMPRINT",FACE,{"disambiguationData":[TD([[makeQuery(id+"F47.imprint","IMPRINT",EDGE,{"derivedFrom":sQuery(id+"F47.wireOp",EDGE,"E83")}),-1.0]])]});
            extrude(context, id + "F48", {"entities" : qUnion([Q0]), "oppositeDirection" : true, "depth" : 1.5 * mm});
        }
        {
            var Q0;
            {var subQ5=sQuery(id+"F47.wireOp",EDGE,"E95");Q0=makeQuery(id+"F47.imprint","IMPRINT",FACE,{"disambiguationData":[TD([[makeQuery(id+"F47.imprint","IMPRINT",EDGE,{"derivedFrom":subQ5}),-1.0]])]});}
            var Q1;
            {var subQ5=sQuery(id+"F47.wireOp",EDGE,"E93");Q1=makeQuery(id+"F47.imprint","IMPRINT",FACE,{"disambiguationData":[TD([[makeQuery(id+"F47.imprint","IMPRINT",EDGE,{"derivedFrom":subQ5}),-1.0]])]});}
            var Q2;
            Q2=makeQuery(id+"F47.imprint","IMPRINT",FACE,{"disambiguationData":[TD([[makeQuery(id+"F47.imprint","IMPRINT",EDGE,{"derivedFrom":sQuery(id+"F47.wireOp",EDGE,"E82")}),-1.0]])]});
            extrude(context, id + "F49", {"entities" : qUnion([Q0, Q1, Q2]), "operationType" : NewBodyOperationType.ADD, "oppositeDirection" : true, "depth" : 5 * mm});
        }
        {
            var Q0;
            Q0=makeQuery(id+"F49.opExtrude","SWEPT_EDGE",EDGE,{"disambiguationData":[OSD([sQuery(id+"F47.wireOp",EDGE,"E94"),sQuery(id+"F47.wireOp",EDGE,"E95")])]});
            var Q1;
            Q1=makeQuery(id+"F49.opExtrude","SWEPT_EDGE",EDGE,{"disambiguationData":[OSD([sQuery(id+"F47.wireOp",EDGE,"E93"),sQuery(id+"F47.wireOp",EDGE,"E94")])]});
            var Q2;
            Q2=makeQuery(id+"F49.opExtrude","SWEPT_EDGE",EDGE,{"disambiguationData":[OSD([sQuery(id+"F47.wireOp",EDGE,"E92"),sQuery(id+"F47.wireOp",EDGE,"E95")])]});
            var Q3;
            Q3=makeQuery(id+"F49.opExtrude","SWEPT_EDGE",EDGE,{"disambiguationData":[OSD([sQuery(id+"F47.wireOp",EDGE,"E92"),sQuery(id+"F47.wireOp",EDGE,"E93")])]});
            var Q4;
            Q4=makeQuery(id+"F48.opExtrude","SWEPT_EDGE",EDGE,{"disambiguationData":[OSD([sQuery(id+"F47.wireOp",EDGE,"E83"),sQuery(id+"F47.wireOp",EDGE,"E84")])]});
            var Q5;
            Q5=makeQuery(id+"F48.opExtrude","SWEPT_EDGE",EDGE,{"disambiguationData":[OSD([sQuery(id+"F47.wireOp",EDGE,"E86"),sQuery(id+"F47.wireOp",EDGE,"E87")])]});
            var Q6;
            Q6=makeQuery(id+"F48.opExtrude","SWEPT_EDGE",EDGE,{"disambiguationData":[OSD([sQuery(id+"F47.wireOp",EDGE,"E83"),sQuery(id+"F47.wireOp",EDGE,"E90")])]});
            var Q7;
            Q7=makeQuery(id+"F48.opExtrude","SWEPT_EDGE",EDGE,{"disambiguationData":[OSD([sQuery(id+"F47.wireOp",EDGE,"E87"),sQuery(id+"F47.wireOp",EDGE,"E88")])]});
            fillet(context, id + "F50", {"entities" : qUnion([Q0, Q1, Q2, Q3, Q4, Q5, Q6, Q7]), "radius" : 0.5 * mm, "tangentPropagation" : true, "allowEdgeOverflow" : false});
        }
        {
            var Q0;
            {var subQ5=sQuery(id+"F47.wireOp",EDGE,"E93");Q0=makeQuery(id+"F47.imprint","IMPRINT",FACE,{"disambiguationData":[TD([[makeQuery(id+"F47.imprint","IMPRINT",EDGE,{"derivedFrom":subQ5}),-1.0]])]});}
            var Q1;
            Q1=makeQuery(id+"F47.imprint","IMPRINT",FACE,{"disambiguationData":[TD([[makeQuery(id+"F47.imprint","IMPRINT",EDGE,{"derivedFrom":sQuery(id+"F47.wireOp",EDGE,"E83")}),-1.0]])]});
            var Q2;
            {var subQ5=sQuery(id+"F47.wireOp",EDGE,"E95");Q2=makeQuery(id+"F47.imprint","IMPRINT",FACE,{"disambiguationData":[TD([[makeQuery(id+"F47.imprint","IMPRINT",EDGE,{"derivedFrom":subQ5}),-1.0]])]});}
            extrude(context, id + "F51", {"entities" : qUnion([Q0, Q1, Q2]), "operationType" : NewBodyOperationType.REMOVE, "oppositeDirection" : true, "depth" : 1 * mm});
        }
        {
            var Q0;
            Q0=makeQuery(id+"F51.boolean.opBoolean","COPY",EDGE,{"derivedFrom":makeQuery(id+"F51.opExtrude","CAP_EDGE",EDGE,{"disambiguationData":[OSD([sQuery(id+"F47.wireOp",EDGE,"E98")])],"isStart":false})});
            fillet(context, id + "F52", {"entities" : qUnion([Q0]), "radius" : 0.5 * mm, "tangentPropagation" : true, "allowEdgeOverflow" : false});
        }
        {
            var Q0;
            Q0=makeQuery(id+"F48.opExtrude","SWEPT_EDGE",EDGE,{"disambiguationData":[OSD([sQuery(id+"F47.wireOp",EDGE,"E84"),sQuery(id+"F47.wireOp",EDGE,"E85")])]});
            var Q1;
            Q1=makeQuery(id+"F48.opExtrude","SWEPT_EDGE",EDGE,{"disambiguationData":[OSD([sQuery(id+"F47.wireOp",EDGE,"E85"),sQuery(id+"F47.wireOp",EDGE,"E86")])]});
            var Q2;
            Q2=makeQuery(id+"F48.opExtrude","SWEPT_EDGE",EDGE,{"disambiguationData":[OSD([sQuery(id+"F47.wireOp",EDGE,"E89"),sQuery(id+"F47.wireOp",EDGE,"E90")])]});
            var Q3;
            Q3=makeQuery(id+"F48.opExtrude","SWEPT_EDGE",EDGE,{"disambiguationData":[OSD([sQuery(id+"F47.wireOp",EDGE,"E88"),sQuery(id+"F47.wireOp",EDGE,"E89")])]});
            fillet(context, id + "F53", {"entities" : qUnion([Q0, Q1, Q2, Q3]), "radius" : 0.1 * mm, "tangentPropagation" : true, "allowEdgeOverflow" : false});
        }
        {
            var Q0;
            {var subQ0=sQuery(id+"F47.wireOp",EDGE,"E92");var subQ1=sQuery(id+"F47.wireOp",EDGE,"E93");var subQ2=sQuery(id+"F47.wireOp",EDGE,"E94");var subQ3=sQuery(id+"F47.wireOp",EDGE,"E95");Q0=makeQuery(id+"F49.boolean.opBoolean","MERGE",FACE,{"derivedFrom":[makeQuery(id+"F48.opExtrude","CAP_FACE",FACE,{"disambiguationData":[OSD([sQuery(id+"F47.wireOp",EDGE,"E83"),sQuery(id+"F47.wireOp",EDGE,"E84"),sQuery(id+"F47.wireOp",EDGE,"E85"),sQuery(id+"F47.wireOp",EDGE,"E86"),sQuery(id+"F47.wireOp",EDGE,"E87"),sQuery(id+"F47.wireOp",EDGE,"E88"),sQuery(id+"F47.wireOp",EDGE,"E89"),sQuery(id+"F47.wireOp",EDGE,"E90"),subQ0,subQ1,subQ2,subQ3])],"isStart":true}),makeQuery(id+"F49.opExtrude","CAP_FACE",FACE,{"disambiguationData":[OSD([sQuery(id+"F47.wireOp",EDGE,"E82"),subQ0,subQ1,subQ2,subQ3])],"isStart":true})]});}
            extrude(context, id + "F54", {"entities" : qUnion([Q0]), "operationType" : NewBodyOperationType.ADD, "oppositeDirection" : true, "depth" : 5.25 * mm});
        }
        {
            var Q0;
            Q0=makeQuery(id+"F54.boolean.opBoolean","INTERSECT",EDGE,{"derivedFrom":[makeQuery(id+"F49.opExtrude","CAP_FACE",FACE,{"disambiguationData":[OSD([sQuery(id+"F47.wireOp",EDGE,"E82"),sQuery(id+"F47.wireOp",EDGE,"E92"),sQuery(id+"F47.wireOp",EDGE,"E93"),sQuery(id+"F47.wireOp",EDGE,"E94"),sQuery(id+"F47.wireOp",EDGE,"E95")])],"isStart":false}),makeQuery(id+"F54.opExtrude","SWEPT_FACE",FACE,{"disambiguationData":[OSD([sQuery(id+"F47.wireOp",EDGE,"E98")])]})]});
            fillet(context, id + "F55", {"entities" : qUnion([Q0]), "radius" : 0.1 * mm, "tangentPropagation" : true, "allowEdgeOverflow" : false});
        }
        {
            var Q0;
            Q0=makeQuery(id+"F49.opExtrude","SWEPT_FACE",FACE,{"disambiguationData":[OSD([sQuery(id+"F47.wireOp",EDGE,"E92")])]});
            var sketch = newSketch(context, id + "F56", { "sketchPlane" : qUnion([Q0])});
            skPoint(sketch, "E99", {"position": v(-46, -21.5) * mm});
            skCircle(sketch, "E100", {"center": v(-46, -23) * mm, "radius": 0.38 * mm});
            skSolve(sketch);
        }
        {
            var Q0;
            Q0=makeQuery(id+"F56.imprint","IMPRINT",FACE,{"disambiguationData":[TD([[makeQuery(id+"F56.imprint","IMPRINT",EDGE,{"derivedFrom":sQuery(id+"F56.wireOp",EDGE,"E100")}),1.0]])]});
            var Q1;
            {var subQ0=sQuery(id+"F47.wireOp",EDGE,"E82");Q1=makeQuery(id+"F54.boolean.opBoolean","MERGE",FACE,{"derivedFrom":[makeQuery(id+"F49.opExtrude","SWEPT_FACE",FACE,{"disambiguationData":[OSD([subQ0])]}),makeQuery(id+"F54.opExtrude","SWEPT_FACE",FACE,{"disambiguationData":[OSD([subQ0])]})]});}
            extrude(context, id + "F57", {"entities" : qUnion([Q0]), "operationType" : NewBodyOperationType.REMOVE, "endBound" : BoundingType.UP_TO_BODY, "oppositeDirection" : true, "endBoundEntityBody" : qUnion([Q1]), "depth" : 25 * mm});
        }
        {
            var Q0;
            Q0=qCreatedBy(id+"F22.planeOp",FACE);
            cPlane(context, id + "F58", {"entities" : qUnion([Q0]), "cplaneType" : CPlaneType.OFFSET, "offset" : 20 * mm, "width" : 150 * mm, "height" : 150 * mm});
        }
        {
            var Q0;
            Q0=qCreatedBy(id+"F58.planeOp",FACE);
            var sketch = newSketch(context, id + "F59", { "sketchPlane" : qUnion([Q0])});
            skLineSegment(sketch, "E101", {"start": v(0, 0) * mm, "end": v(52.5, 0) * mm, "construction": true});
            skSolve(sketch);
        }
        {
            var Q0;
            Q0=qCreatedBy(makeId("Front.planeOp"),FACE);
            var sketch = newSketch(context, id + "F60", { "sketchPlane" : qUnion([Q0])});
            skLineSegment(sketch, "E102", {"start": v(52.5, 40) * mm, "end": v(52.5, 65.44) * mm, "construction": true});
            skLineSegment(sketch, "E103", {"start": v(52.5, 40) * mm, "end": v(53.5, 40) * mm});
            skLineSegment(sketch, "E104", {"start": v(53.5, 40) * mm, "end": v(53.5, 45) * mm});
            skLineSegment(sketch, "E105", {"start": v(53.5, 45) * mm, "end": v(54.12, 45) * mm});
            skLineSegment(sketch, "E106", {"start": v(54.12, 45) * mm, "end": v(54.12, 46) * mm});
            skLineSegment(sketch, "E107", {"start": v(53.63, 46.25) * mm, "end": v(52.5, 46.25) * mm});
            skLineSegment(sketch, "E108", {"start": v(52.5, 46.25) * mm, "end": v(52.5, 40) * mm});
            skLineSegment(sketch, "E109", {"start": v(53.63, 46.25) * mm, "end": v(53.63, 46) * mm});
            skLineSegment(sketch, "E110", {"start": v(53.63, 46) * mm, "end": v(54.12, 46) * mm});
            skSolve(sketch);
        }
        {
            var Q0;
            Q0=makeQuery(id+"F60.imprint","IMPRINT",FACE,{"disambiguationData":[TD([[makeQuery(id+"F60.imprint","IMPRINT",EDGE,{"derivedFrom":sQuery(id+"F60.wireOp",EDGE,"E103")}),1.0]])]});
            var Q1;
            Q1=sQuery(id+"F60.wireOp",EDGE,"E102");
            revolve(context, id + "F61", {"entities" : qUnion([Q0]), "axis" : qUnion([Q1]), "revolveType" : RevolveType.FULL});
        }
        {
            var Q0;
            Q0=makeQuery(id+"F61.opRevolve","SWEPT_FACE",FACE,{"disambiguationData":[OSD([sQuery(id+"F60.wireOp",EDGE,"E110")])]});
            var sketch = newSketch(context, id + "F62", { "sketchPlane" : qUnion([Q0])});
            skLineSegment(sketch, "E111", {"start": v(53.87, 0.87) * mm, "end": v(53.87, -0.87) * mm});
            skLineSegment(sketch, "E112", {"start": v(51.12, 0.87) * mm, "end": v(51.12, -0.87) * mm});
            skSolve(sketch);
        }
        {
            var Q0;
            {var subQ1=sQuery(id+"F62.wireOp",EDGE,"E112");Q0=makeQuery(id+"F62.imprint","IMPRINT",FACE,{"disambiguationData":[TD([[makeQuery(id+"F62.imprint","IMPRINT",EDGE,{"derivedFrom":subQ1}),-1.0]])]});}
            var Q1;
            {var subQ1=sQuery(id+"F62.wireOp",EDGE,"E111");Q1=makeQuery(id+"F62.imprint","IMPRINT",FACE,{"disambiguationData":[TD([[makeQuery(id+"F62.imprint","IMPRINT",EDGE,{"derivedFrom":subQ1}),1.0]])]});}
            extrude(context, id + "F63", {"entities" : qUnion([Q0, Q1]), "operationType" : NewBodyOperationType.REMOVE, "oppositeDirection" : true, "depth" : 0.75 * mm});
        }
        {
            var Q0;
            {var subQ0=makeQuery(id+"F61.opRevolve","SWEPT_EDGE",EDGE,{"disambiguationData":[OSD([sQuery(id+"F60.wireOp",EDGE,"E106"),sQuery(id+"F60.wireOp",EDGE,"E110")])]});Q0=qUnion([makeQuery(id+"F63.boolean.opBoolean","SPLIT",EDGE,{"disambiguationData":[OD(0.0)],"derivedFrom":subQ0}),makeQuery(id+"F63.boolean.opBoolean","SPLIT",EDGE,{"disambiguationData":[OD(1.0)],"derivedFrom":subQ0})]);}
            var Q1;
            Q1=makeQuery(id+"F61.opRevolve","SWEPT_EDGE",EDGE,{"disambiguationData":[OSD([sQuery(id+"F60.wireOp",EDGE,"E107"),sQuery(id+"F60.wireOp",EDGE,"E109")])]});
            fillet(context, id + "F64", {"entities" : qUnion([Q0, Q1]), "radius" : 0.1 * mm, "tangentPropagation" : true, "allowEdgeOverflow" : false});
        }
    });
